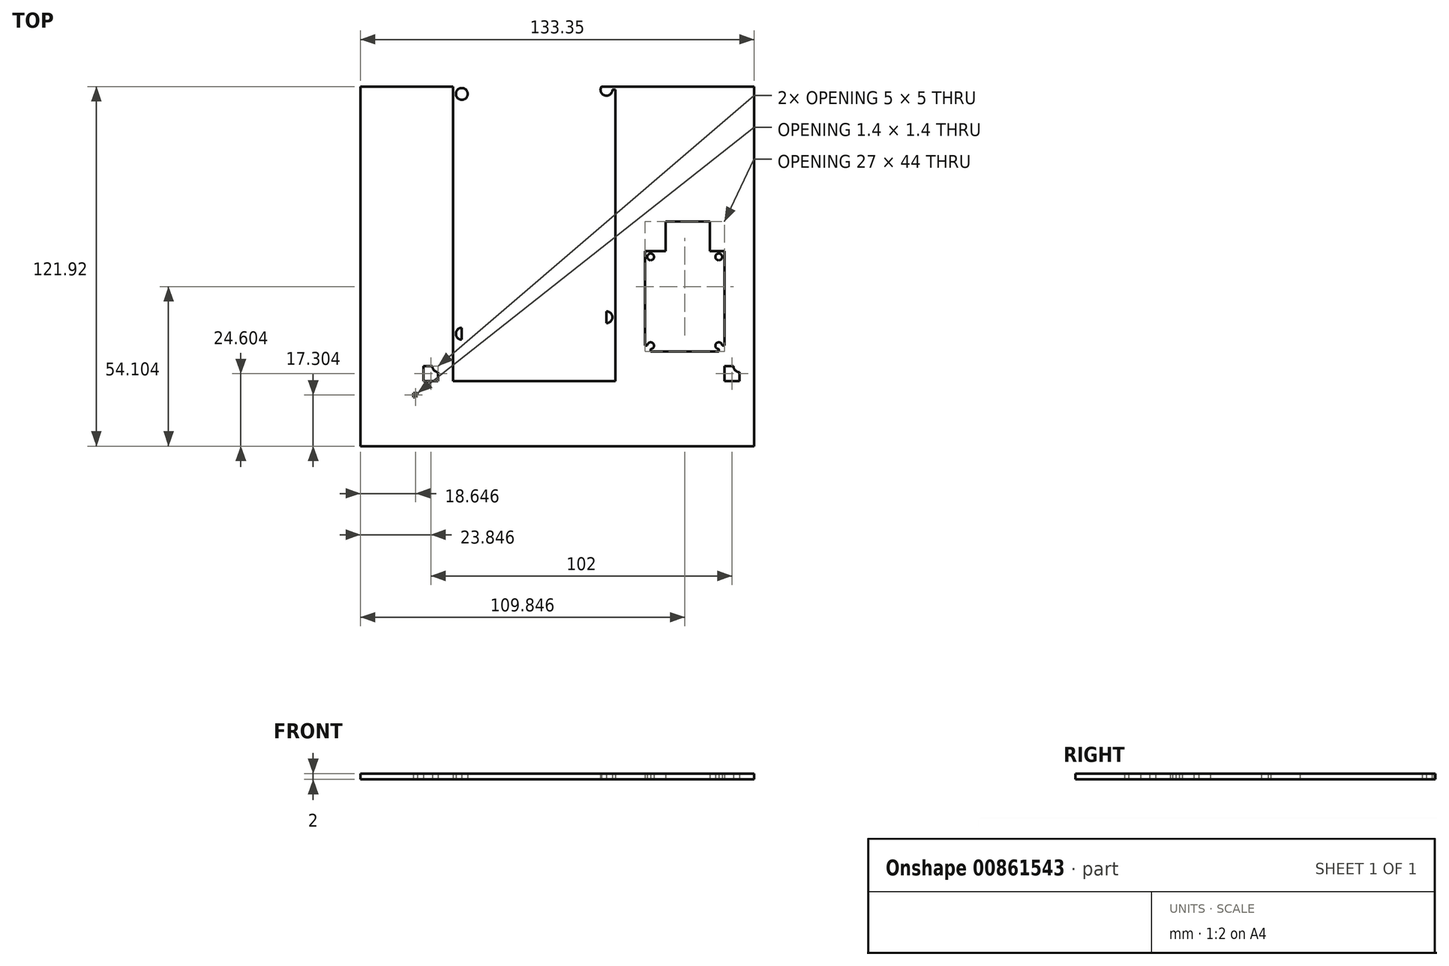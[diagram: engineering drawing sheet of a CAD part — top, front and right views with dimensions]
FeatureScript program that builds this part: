
annotation { "Feature Type Name" : "Feature", "Feature Type Description" : "" }
export const myFeature = defineFeature(function(context is Context, id is Id, definition is map)
    precondition{}
    {
        {
            var Q0;
            Q0=qCreatedBy(makeId("Top.planeOp"),FACE);
            var sketch = newSketch(context, id + "F0", { "sketchPlane" : qUnion([Q0])});
            skLineSegment(sketch, "E0.bottom", {"start": v(-139.34, -1.26) * mm, "end": v(-129.34, -1.26) * mm});
            skLineSegment(sketch, "E0.top", {"start": v(-139.34, -11.26) * mm, "end": v(-129.34, -11.26) * mm});
            skLineSegment(sketch, "E0.left", {"start": v(-139.34, -1.26) * mm, "end": v(-139.34, -11.26) * mm});
            skLineSegment(sketch, "E0.right", {"start": v(-129.34, -1.26) * mm, "end": v(-129.34, -11.26) * mm});
            skLineSegment(sketch, "E1.bottom", {"start": v(-129.34, -11.26) * mm, "end": v(-74.34, -11.26) * mm});
            skLineSegment(sketch, "E1.top", {"start": v(-129.34, -114.76) * mm, "end": v(-74.34, -114.76) * mm});
            skLineSegment(sketch, "E1.left", {"start": v(-129.34, -11.26) * mm, "end": v(-129.34, -114.76) * mm});
            skLineSegment(sketch, "E1.right", {"start": v(-74.34, -11.26) * mm, "end": v(-74.34, -114.76) * mm});
            skLineSegment(sketch, "E2", {"start": v(-74.34, -114.76) * mm, "end": v(-64.34, -114.76) * mm});
            skLineSegment(sketch, "E3.bottom", {"start": v(-64.34, -114.76) * mm, "end": v(-37.34, -114.76) * mm});
            skLineSegment(sketch, "E3.top", {"start": v(-64.34, -80.76) * mm, "end": v(-37.34, -80.76) * mm});
            skLineSegment(sketch, "E3.left", {"start": v(-64.34, -114.76) * mm, "end": v(-64.34, -80.76) * mm});
            skLineSegment(sketch, "E3.right", {"start": v(-37.34, -114.76) * mm, "end": v(-37.34, -80.76) * mm});
            skLineSegment(sketch, "E4", {"start": v(-37.34, -80.76) * mm, "end": v(-42.34, -80.76) * mm});
            skLineSegment(sketch, "E5.bottom", {"start": v(-42.34, -80.76) * mm, "end": v(-57.34, -80.76) * mm});
            skLineSegment(sketch, "E5.top", {"start": v(-42.34, -70.76) * mm, "end": v(-57.34, -70.76) * mm});
            skLineSegment(sketch, "E5.left", {"start": v(-42.34, -80.76) * mm, "end": v(-42.34, -70.76) * mm});
            skLineSegment(sketch, "E5.right", {"start": v(-57.34, -80.76) * mm, "end": v(-57.34, -70.76) * mm});
            skLineSegment(sketch, "E6", {"start": v(-64.34, -80.76) * mm, "end": v(-64.34, -60.76) * mm});
            skLineSegment(sketch, "E7.bottom", {"start": v(-64.34, -60.76) * mm, "end": v(-37.84, -60.76) * mm});
            skLineSegment(sketch, "E7.top", {"start": v(-64.34, -24.76) * mm, "end": v(-37.84, -24.76) * mm});
            skLineSegment(sketch, "E7.left", {"start": v(-64.34, -60.76) * mm, "end": v(-64.34, -24.76) * mm});
            skLineSegment(sketch, "E7.right", {"start": v(-37.84, -60.76) * mm, "end": v(-37.84, -24.76) * mm});
            skLineSegment(sketch, "E8", {"start": v(-74.34, -11.26) * mm, "end": v(-27.34, -11.26) * mm});
            skLineSegment(sketch, "E9.bottom", {"start": v(-129.34, -114.76) * mm, "end": v(-139.34, -114.76) * mm});
            skLineSegment(sketch, "E9.top", {"start": v(-129.34, -124.76) * mm, "end": v(-139.34, -124.76) * mm});
            skLineSegment(sketch, "E9.left", {"start": v(-129.34, -114.76) * mm, "end": v(-129.34, -124.76) * mm});
            skLineSegment(sketch, "E9.right", {"start": v(-139.34, -114.76) * mm, "end": v(-139.34, -124.76) * mm});
            skLineSegment(sketch, "E10.bottom", {"start": v(-37.34, -114.76) * mm, "end": v(-27.34, -114.76) * mm});
            skLineSegment(sketch, "E10.top", {"start": v(-37.34, -124.76) * mm, "end": v(-27.34, -124.76) * mm});
            skLineSegment(sketch, "E10.left", {"start": v(-37.34, -114.76) * mm, "end": v(-37.34, -124.76) * mm});
            skLineSegment(sketch, "E10.right", {"start": v(-27.34, -114.76) * mm, "end": v(-27.34, -124.76) * mm});
            skLineSegment(sketch, "E11.top", {"start": v(-139.34, -124.76) * mm, "end": v(-37.34, -124.76) * mm});
            skLineSegment(sketch, "E12", {"start": v(-129.34, -11.26) * mm, "end": v(-124.34, -11.26) * mm});
            skLineSegment(sketch, "E13", {"start": v(-124.34, -11.26) * mm, "end": v(-124.34, -1.26) * mm});
            skLineSegment(sketch, "E14", {"start": v(-74.34, -11.26) * mm, "end": v(-79.34, -11.26) * mm});
            skLineSegment(sketch, "E15", {"start": v(-79.34, -11.26) * mm, "end": v(-79.34, -1.26) * mm});
            skLineSegment(sketch, "E16.bottom", {"start": v(-129.34, -11.26) * mm, "end": v(-126.54, -11.26) * mm});
            skLineSegment(sketch, "E16.left", {"start": v(-129.34, -11.26) * mm, "end": v(-129.34, -14.06) * mm});
            skLineSegment(sketch, "E17.bottom", {"start": v(-129.34, -114.76) * mm, "end": v(-126.34, -114.76) * mm});
            skLineSegment(sketch, "E17.left", {"start": v(-129.34, -114.76) * mm, "end": v(-129.34, -111.76) * mm});
            skLineSegment(sketch, "E18.bottom", {"start": v(-74.34, -114.76) * mm, "end": v(-77.2, -114.76) * mm});
            skLineSegment(sketch, "E18.left", {"start": v(-74.34, -114.76) * mm, "end": v(-74.34, -111.9) * mm});
            skLineSegment(sketch, "E19.bottom", {"start": v(-74.34, -11.26) * mm, "end": v(-77.34, -11.26) * mm});
            skLineSegment(sketch, "E19.left", {"start": v(-74.34, -11.26) * mm, "end": v(-74.34, -14.26) * mm});
            skLineSegment(sketch, "E20.left", {"start": v(-27.34, -11.26) * mm, "end": v(-27.34, -14.66) * mm});
            skLineSegment(sketch, "E21.bottom", {"start": v(-37.84, -60.76) * mm, "end": v(-39.6, -60.76) * mm});
            skLineSegment(sketch, "E21.left", {"start": v(-37.84, -60.76) * mm, "end": v(-37.84, -59) * mm});
            skLineSegment(sketch, "E22.bottom", {"start": v(-37.84, -24.76) * mm, "end": v(-39.54, -24.76) * mm});
            skLineSegment(sketch, "E22.top", {"start": v(-37.84, -26.46) * mm, "end": v(-39.54, -26.46) * mm});
            skLineSegment(sketch, "E22.left", {"start": v(-37.84, -24.76) * mm, "end": v(-37.84, -26.46) * mm});
            skLineSegment(sketch, "E22.right", {"start": v(-39.54, -24.76) * mm, "end": v(-39.54, -26.46) * mm});
            skLineSegment(sketch, "E23.bottom", {"start": v(-64.34, -24.76) * mm, "end": v(-62.64, -24.76) * mm});
            skLineSegment(sketch, "E23.top", {"start": v(-64.34, -26.46) * mm, "end": v(-62.64, -26.46) * mm});
            skLineSegment(sketch, "E23.left", {"start": v(-64.34, -24.76) * mm, "end": v(-64.34, -26.46) * mm});
            skLineSegment(sketch, "E23.right", {"start": v(-62.64, -24.76) * mm, "end": v(-62.64, -26.46) * mm});
            skLineSegment(sketch, "E24.bottom", {"start": v(-64.34, -60.76) * mm, "end": v(-62.6, -60.76) * mm});
            skLineSegment(sketch, "E24.left", {"start": v(-64.34, -60.76) * mm, "end": v(-64.34, -59) * mm});
            skLineSegment(sketch, "E25.bottom", {"start": v(-64.34, -114.76) * mm, "end": v(-62.4, -114.76) * mm});
            skLineSegment(sketch, "E25.top", {"start": v(-64.34, -112.8) * mm, "end": v(-62.4, -112.8) * mm});
            skLineSegment(sketch, "E25.left", {"start": v(-64.34, -114.76) * mm, "end": v(-64.34, -112.8) * mm});
            skLineSegment(sketch, "E25.right", {"start": v(-62.4, -114.76) * mm, "end": v(-62.4, -112.8) * mm});
            skLineSegment(sketch, "E26.bottom", {"start": v(-37.34, -114.76) * mm, "end": v(-39.3, -114.76) * mm});
            skLineSegment(sketch, "E26.top", {"start": v(-37.34, -112.8) * mm, "end": v(-39.3, -112.8) * mm});
            skLineSegment(sketch, "E26.left", {"start": v(-37.34, -114.76) * mm, "end": v(-37.34, -112.8) * mm});
            skLineSegment(sketch, "E26.right", {"start": v(-39.3, -114.76) * mm, "end": v(-39.3, -112.8) * mm});
            skLineSegment(sketch, "E27.bottom", {"start": v(-37.34, -80.76) * mm, "end": v(-39.3, -80.76) * mm});
            skLineSegment(sketch, "E27.top", {"start": v(-37.34, -82.7) * mm, "end": v(-39.3, -82.7) * mm});
            skLineSegment(sketch, "E27.left", {"start": v(-37.34, -80.76) * mm, "end": v(-37.34, -82.7) * mm});
            skLineSegment(sketch, "E27.right", {"start": v(-39.3, -80.76) * mm, "end": v(-39.3, -82.7) * mm});
            skLineSegment(sketch, "E28.bottom", {"start": v(-64.34, -80.76) * mm, "end": v(-62.4, -80.76) * mm});
            skLineSegment(sketch, "E28.top", {"start": v(-64.34, -82.7) * mm, "end": v(-62.4, -82.7) * mm});
            skLineSegment(sketch, "E28.left", {"start": v(-64.34, -80.76) * mm, "end": v(-64.34, -82.7) * mm});
            skLineSegment(sketch, "E28.right", {"start": v(-62.4, -80.76) * mm, "end": v(-62.4, -82.7) * mm});
            skCircle(sketch, "E29", {"center": v(-39.3, -112.8) * mm, "radius": 1.15 * mm});
            skCircle(sketch, "E30", {"center": v(-62.4, -112.8) * mm, "radius": 1.15 * mm});
            skCircle(sketch, "E31", {"center": v(-62.4, -82.7) * mm, "radius": 1.15 * mm});
            skCircle(sketch, "E32", {"center": v(-39.3, -82.7) * mm, "radius": 1.15 * mm});
            skCircle(sketch, "E33", {"center": v(-62.64, -26.46) * mm, "radius": 1.2 * mm});
            skCircle(sketch, "E34", {"center": v(-39.54, -26.46) * mm, "radius": 1.2 * mm});
            skLineSegment(sketch, "E35.top", {"start": v(-37.34, -124.76) * mm, "end": v(-139.34, -124.76) * mm});
            skLineSegment(sketch, "E36.bottom", {"start": v(-139.34, -124.76) * mm, "end": v(-134.34, -124.76) * mm});
            skLineSegment(sketch, "E36.top", {"start": v(-139.34, -119.76) * mm, "end": v(-134.34, -119.76) * mm});
            skLineSegment(sketch, "E36.left", {"start": v(-139.34, -124.76) * mm, "end": v(-139.34, -119.76) * mm});
            skLineSegment(sketch, "E36.right", {"start": v(-134.34, -124.76) * mm, "end": v(-134.34, -119.76) * mm});
            skCircle(sketch, "E37", {"center": v(-134.34, -119.76) * mm, "radius": 2 * mm});
            skLineSegment(sketch, "E38.bottom", {"start": v(-37.34, -124.76) * mm, "end": v(-32.34, -124.76) * mm});
            skLineSegment(sketch, "E38.top", {"start": v(-37.34, -119.76) * mm, "end": v(-32.34, -119.76) * mm});
            skLineSegment(sketch, "E38.left", {"start": v(-37.34, -124.76) * mm, "end": v(-37.34, -119.76) * mm});
            skLineSegment(sketch, "E38.right", {"start": v(-32.34, -124.76) * mm, "end": v(-32.34, -119.76) * mm});
            skCircle(sketch, "E39", {"center": v(-32.34, -119.76) * mm, "radius": 2 * mm});
            skLineSegment(sketch, "E40.bottom", {"start": v(-139.34, -1.26) * mm, "end": v(-134.34, -1.26) * mm});
            skLineSegment(sketch, "E40.top", {"start": v(-139.34, -6.26) * mm, "end": v(-134.34, -6.26) * mm});
            skLineSegment(sketch, "E40.left", {"start": v(-139.34, -1.26) * mm, "end": v(-139.34, -6.26) * mm});
            skLineSegment(sketch, "E40.right", {"start": v(-134.34, -1.26) * mm, "end": v(-134.34, -6.26) * mm});
            skCircle(sketch, "E41", {"center": v(-134.34, -6.26) * mm, "radius": 2 * mm});
            skLineSegment(sketch, "E42.bottom", {"start": v(-129.34, -11.26) * mm, "end": v(-126.34, -11.26) * mm});
            skLineSegment(sketch, "E42.left", {"start": v(-129.34, -11.26) * mm, "end": v(-129.34, -27.96) * mm});
            skLineSegment(sketch, "E43.top", {"start": v(-129.34, -108.76) * mm, "end": v(-126.34, -108.76) * mm});
            skLineSegment(sketch, "E43.left", {"start": v(-129.34, -114.76) * mm, "end": v(-129.34, -108.76) * mm});
            skLineSegment(sketch, "E43.right", {"start": v(-126.34, -114.76) * mm, "end": v(-126.34, -108.76) * mm});
            skLineSegment(sketch, "E44.bottom", {"start": v(-74.34, -114.76) * mm, "end": v(-77.34, -114.76) * mm});
            skLineSegment(sketch, "E44.top", {"start": v(-74.34, -103.16) * mm, "end": v(-77.34, -103.16) * mm});
            skLineSegment(sketch, "E44.left", {"start": v(-74.34, -114.76) * mm, "end": v(-74.34, -103.16) * mm});
            skLineSegment(sketch, "E44.right", {"start": v(-77.34, -114.76) * mm, "end": v(-77.34, -103.16) * mm});
            skLineSegment(sketch, "E45.top", {"start": v(-74.34, -26.06) * mm, "end": v(-77.34, -26.06) * mm});
            skLineSegment(sketch, "E45.left", {"start": v(-74.34, -114.76) * mm, "end": v(-74.34, -26.06) * mm});
            skLineSegment(sketch, "E45.right", {"start": v(-77.34, -114.76) * mm, "end": v(-77.34, -26.06) * mm});
            skLineSegment(sketch, "E46.top", {"start": v(-129.34, -27.46) * mm, "end": v(-126.34, -27.46) * mm});
            skLineSegment(sketch, "E46.left", {"start": v(-129.34, -114.76) * mm, "end": v(-129.34, -27.46) * mm});
            skLineSegment(sketch, "E46.right", {"start": v(-126.34, -114.76) * mm, "end": v(-126.34, -27.46) * mm});
            skCircle(sketch, "E47", {"center": v(-126.34, -108.76) * mm, "radius": 2 * mm});
            skCircle(sketch, "E48", {"center": v(-126.34, -27.46) * mm, "radius": 2 * mm});
            skCircle(sketch, "E49", {"center": v(-77.34, -26.06) * mm, "radius": 2 * mm});
            skCircle(sketch, "E50", {"center": v(-77.34, -103.16) * mm, "radius": 2 * mm});
            skLineSegment(sketch, "E51", {"start": v(-139.34, -1.26) * mm, "end": v(-83.34, -1.26) * mm});
            skLineSegment(sketch, "E52.bottom", {"start": v(-83.34, -1.26) * mm, "end": v(-139.34, -1.26) * mm});
            skLineSegment(sketch, "E53.MirrorCS", {"start": v(-139.5, -132.26) * mm, "end": v(-139.5, -11.26) * mm});
            skLineSegment(sketch, "E54.MirrorCS", {"start": v(-221.34, -11.26) * mm, "end": v(-139.34, -11.26) * mm});
            skLineSegment(sketch, "E55.MirrorCS", {"start": v(-221.34, -132.26) * mm, "end": v(-139.34, -132.26) * mm});
            skCircle(sketch, "E56.MirrorC", {"center": v(-142.74, -128.86) * mm, "radius": 1.4 * mm});
            skCircle(sketch, "E57.MirrorC", {"center": v(-217.94, -128.86) * mm, "radius": 1.7 * mm});
            skCircle(sketch, "E58.MirrorC", {"center": v(-217.94, -14.66) * mm, "radius": 1.4 * mm});
            skCircle(sketch, "E59.MirrorC", {"center": v(-142.74, -14.66) * mm, "radius": 1.4 * mm});
            skLineSegment(sketch, "E60.MirrorCS", {"start": v(-142.74, -11.26) * mm, "end": v(-142.74, -14.66) * mm});
            skLineSegment(sketch, "E61.MirrorCS", {"start": v(-139.34, -14.66) * mm, "end": v(-142.74, -14.66) * mm});
            skLineSegment(sketch, "E62.MirrorCS", {"start": v(-217.94, -11.26) * mm, "end": v(-217.94, -14.66) * mm});
            skLineSegment(sketch, "E63.MirrorCS", {"start": v(-221.34, -14.66) * mm, "end": v(-217.94, -14.66) * mm});
            skLineSegment(sketch, "E64.MirrorCS", {"start": v(-142.74, -132.26) * mm, "end": v(-142.74, -128.86) * mm});
            skLineSegment(sketch, "E65.MirrorCS", {"start": v(-139.34, -128.86) * mm, "end": v(-142.74, -128.86) * mm});
            skLineSegment(sketch, "E66.MirrorCS", {"start": v(-221.34, -128.86) * mm, "end": v(-217.94, -128.86) * mm});
            skLineSegment(sketch, "E67.MirrorCS", {"start": v(-217.94, -132.26) * mm, "end": v(-217.94, -128.86) * mm});
            skLineSegment(sketch, "E68.MirrorCS", {"start": v(-27.34, -1.26) * mm, "end": v(-231.34, -1.26) * mm});
            skLineSegment(sketch, "E69", {"start": v(-221.34, -11.26) * mm, "end": v(-221.34, -1.26) * mm});
            skLineSegment(sketch, "E70", {"start": v(-221.34, -132.26) * mm, "end": v(-221.34, -11.26) * mm});
            skLineSegment(sketch, "E71", {"start": v(-221.34, -132.26) * mm, "end": v(-231.5, -132.26) * mm});
            skLineSegment(sketch, "E72", {"start": v(-27.34, -11.26) * mm, "end": v(-27.34, -1.26) * mm});
            skLineSegment(sketch, "E73.bottom", {"start": v(-221.34, -132.26) * mm, "end": v(-231.34, -132.26) * mm});
            skLineSegment(sketch, "E73.top", {"start": v(-221.34, -142.26) * mm, "end": v(-231.34, -142.26) * mm});
            skLineSegment(sketch, "E73.left", {"start": v(-221.34, -132.26) * mm, "end": v(-221.34, -142.26) * mm});
            skLineSegment(sketch, "E73.right", {"start": v(-231.34, -132.26) * mm, "end": v(-231.34, -142.26) * mm});
            skLineSegment(sketch, "E74.bottom", {"start": v(-221.34, -142.26) * mm, "end": v(-139.34, -142.26) * mm});
            skLineSegment(sketch, "E74.left", {"start": v(-221.34, -142.26) * mm, "end": v(-221.34, -132.26) * mm});
            skLineSegment(sketch, "E75", {"start": v(-27.34, -114.76) * mm, "end": v(-27.34, -11.26) * mm});
            skLineSegment(sketch, "E76", {"start": v(-231.34, -132.26) * mm, "end": v(-231.34, -1.26) * mm});
            skLineSegment(sketch, "E77.bottom", {"start": v(-129.34, -124.76) * mm, "end": v(-139.2, -124.76) * mm});
            skLineSegment(sketch, "E77.top", {"start": v(-129.34, -142.26) * mm, "end": v(-139.34, -142.26) * mm});
            skLineSegment(sketch, "E77.left", {"start": v(-129.34, -124.76) * mm, "end": v(-129.34, -142.26) * mm});
            skLineSegment(sketch, "E78", {"start": v(-139.34, -142.26) * mm, "end": v(-139.5, -132.26) * mm});
            skLineSegment(sketch, "E79.bottom", {"start": v(-231.34, -142.26) * mm, "end": v(-226.34, -142.26) * mm});
            skLineSegment(sketch, "E79.top", {"start": v(-231.34, -137.4) * mm, "end": v(-226.34, -137.4) * mm});
            skLineSegment(sketch, "E79.left", {"start": v(-231.34, -142.26) * mm, "end": v(-231.34, -137.4) * mm});
            skLineSegment(sketch, "E79.right", {"start": v(-226.34, -142.26) * mm, "end": v(-226.34, -137.4) * mm});
            skCircle(sketch, "E80", {"center": v(-226.34, -137.4) * mm, "radius": 2 * mm});
            skLineSegment(sketch, "E81.bottom", {"start": v(-221.34, -11.26) * mm, "end": v(-226.34, -11.26) * mm});
            skLineSegment(sketch, "E81.top", {"start": v(-221.34, -6.26) * mm, "end": v(-226.34, -6.26) * mm});
            skLineSegment(sketch, "E81.left", {"start": v(-221.34, -11.26) * mm, "end": v(-221.34, -6.26) * mm});
            skLineSegment(sketch, "E81.right", {"start": v(-226.34, -11.26) * mm, "end": v(-226.34, -6.26) * mm});
            skCircle(sketch, "E82", {"center": v(-226.34, -6.26) * mm, "radius": 2 * mm});
            skLineSegment(sketch, "E83.bottom", {"start": v(-27.34, -11.26) * mm, "end": v(-32.34, -11.26) * mm});
            skLineSegment(sketch, "E83.top", {"start": v(-27.34, -6.26) * mm, "end": v(-32.34, -6.26) * mm});
            skLineSegment(sketch, "E83.left", {"start": v(-27.34, -11.26) * mm, "end": v(-27.34, -6.26) * mm});
            skLineSegment(sketch, "E83.right", {"start": v(-32.34, -11.26) * mm, "end": v(-32.34, -6.26) * mm});
            skCircle(sketch, "E84", {"center": v(-32.34, -6.26) * mm, "radius": 2 * mm});
            skLineSegment(sketch, "E85.bottom", {"start": v(-129.34, -142.26) * mm, "end": v(-77.34, -142.26) * mm});
            skLineSegment(sketch, "E85.top", {"start": v(-129.34, -114.76) * mm, "end": v(-77.34, -114.76) * mm});
            skLineSegment(sketch, "E85.left", {"start": v(-129.34, -142.26) * mm, "end": v(-129.34, -114.76) * mm});
            skLineSegment(sketch, "E86.bottom", {"start": v(-129.34, -142.26) * mm, "end": v(-74.34, -142.26) * mm});
            skLineSegment(sketch, "E86.right", {"start": v(-74.34, -142.26) * mm, "end": v(-74.34, -114.76) * mm});
            skLineSegment(sketch, "E87", {"start": v(-37.84, -24.76) * mm, "end": v(-27.34, -24.94) * mm});
            skLineSegment(sketch, "E88.bottom", {"start": v(-27.34, -24.94) * mm, "end": v(-160.7, -24.94) * mm});
            skLineSegment(sketch, "E88.top", {"start": v(-27.34, -146.86) * mm, "end": v(-160.7, -146.86) * mm});
            skLineSegment(sketch, "E88.left", {"start": v(-27.34, -24.94) * mm, "end": v(-27.34, -146.86) * mm});
            skLineSegment(sketch, "E88.right", {"start": v(-160.7, -24.94) * mm, "end": v(-160.7, -146.86) * mm});
            skSolve(sketch);
        }
        {
            var Q0;
            {var subQ5=sQuery(id+"F0.wireOp",EDGE,"E65.MirrorCS");var subQ7=sQuery(id+"F0.wireOp",EDGE,"E53.MirrorCS");var subQ8=makeQuery(id+"F0.imprint","INTERSECT",VERTEX,{"derivedFrom":[subQ7,subQ5]});Q0=makeQuery(id+"F0.imprint","IMPRINT",FACE,{"disambiguationData":[TD([[makeQuery(id+"F0.imprint","IMPRINT",EDGE,{"disambiguationData":[TD([[subQ8,-1.0]])],"derivedFrom":subQ7}),1.0]])]});}
            var Q1;
            {var subQ1=sQuery(id+"F0.wireOp",EDGE,"E45.right");var subQ16=sQuery(id+"F0.wireOp",EDGE,"E1.top");var subQ17=makeQuery(id+"F0.imprint","INTERSECT",VERTEX,{"derivedFrom":[subQ1,subQ16]});Q1=makeQuery(id+"F0.imprint","IMPRINT",FACE,{"disambiguationData":[TD([[makeQuery(id+"F0.imprint","IMPRINT",EDGE,{"disambiguationData":[TD([[subQ17,-1.0]])],"derivedFrom":subQ1}),1.0]])]});}
            var Q2;
            {var subQ6=sQuery(id+"F0.wireOp",EDGE,"E9.bottom");Q2=makeQuery(id+"F0.imprint","IMPRINT",FACE,{"disambiguationData":[TD([[makeQuery(id+"F0.imprint","IMPRINT",EDGE,{"derivedFrom":subQ6}),-1.0]])]});}
            var Q3;
            {var subQ0=sQuery(id+"F0.wireOp",EDGE,"E46.left");var subQ3=makeQuery(id+"F0.imprint","IMPRINT",VERTEX,{"disambiguationData":[OD(1.0)],"derivedFrom":subQ0});Q3=makeQuery(id+"F0.imprint","IMPRINT",FACE,{"disambiguationData":[TD([[makeQuery(id+"F0.imprint","IMPRINT",EDGE,{"disambiguationData":[TD([[subQ3,1.0]])],"derivedFrom":subQ0}),-1.0]])]});}
            var Q4;
            {var subQ0=sQuery(id+"F0.wireOp",EDGE,"E46.right");var subQ1=sQuery(id+"F0.wireOp",EDGE,"E46.top");var subQ2=makeQuery(id+"F0.imprint","INTERSECT",VERTEX,{"derivedFrom":[subQ1,subQ0]});Q4=makeQuery(id+"F0.imprint","IMPRINT",FACE,{"disambiguationData":[TD([[makeQuery(id+"F0.imprint","IMPRINT",EDGE,{"disambiguationData":[TD([[subQ2,1.0]])],"derivedFrom":subQ1}),1.0]])]});}
            var Q5;
            {var subQ0=sQuery(id+"F0.wireOp",EDGE,"E46.right");var subQ1=sQuery(id+"F0.wireOp",EDGE,"E46.top");var subQ2=makeQuery(id+"F0.imprint","INTERSECT",VERTEX,{"derivedFrom":[subQ1,subQ0]});Q5=makeQuery(id+"F0.imprint","IMPRINT",FACE,{"disambiguationData":[TD([[makeQuery(id+"F0.imprint","IMPRINT",EDGE,{"disambiguationData":[TD([[subQ2,1.0]])],"derivedFrom":subQ1}),-1.0]])]});}
            var Q6;
            {var subQ1=sQuery(id+"F0.wireOp",EDGE,"E45.right");var subQ5=sQuery(id+"F0.wireOp",EDGE,"E45.top");var subQ6=makeQuery(id+"F0.imprint","INTERSECT",VERTEX,{"derivedFrom":[subQ5,subQ1]});Q6=makeQuery(id+"F0.imprint","IMPRINT",FACE,{"disambiguationData":[TD([[makeQuery(id+"F0.imprint","IMPRINT",EDGE,{"disambiguationData":[TD([[subQ6,1.0]])],"derivedFrom":subQ5}),-1.0]])]});}
            var Q7;
            {var subQ0=sQuery(id+"F0.wireOp",EDGE,"E45.left");var subQ3=sQuery(id+"F0.wireOp",EDGE,"E44.top");var subQ4=makeQuery(id+"F0.imprint","INTERSECT",VERTEX,{"derivedFrom":[subQ3,subQ0]});Q7=makeQuery(id+"F0.imprint","IMPRINT",FACE,{"disambiguationData":[TD([[makeQuery(id+"F0.imprint","IMPRINT",EDGE,{"disambiguationData":[TD([[subQ4,-1.0]])],"derivedFrom":subQ3}),-1.0]])]});}
            var Q8;
            {var subQ1=sQuery(id+"F0.wireOp",EDGE,"E2");Q8=makeQuery(id+"F0.imprint","IMPRINT",FACE,{"disambiguationData":[TD([[makeQuery(id+"F0.imprint","IMPRINT",EDGE,{"derivedFrom":subQ1}),1.0]])]});}
            var Q9;
            {var subQ0=sQuery(id+"F0.wireOp",EDGE,"E45.right");var subQ1=sQuery(id+"F0.wireOp",EDGE,"E45.top");var subQ2=makeQuery(id+"F0.imprint","INTERSECT",VERTEX,{"derivedFrom":[subQ1,subQ0]});Q9=makeQuery(id+"F0.imprint","IMPRINT",FACE,{"disambiguationData":[TD([[makeQuery(id+"F0.imprint","IMPRINT",EDGE,{"disambiguationData":[TD([[subQ2,1.0]])],"derivedFrom":subQ1}),1.0]])]});}
            var Q10;
            Q10=makeQuery(id+"F0.imprint","IMPRINT",FACE,{"disambiguationData":[TD([[makeQuery(id+"F0.imprint","IMPRINT",EDGE,{"derivedFrom":sQuery(id+"F0.wireOp",EDGE,"E7.bottom")}),1.0]])]});
            var Q11;
            {var subQ0=sQuery(id+"F0.wireOp",EDGE,"E23.right");var subQ1=sQuery(id+"F0.wireOp",EDGE,"E23.top");var subQ2=makeQuery(id+"F0.imprint","INTERSECT",VERTEX,{"derivedFrom":[subQ1,subQ0]});Q11=makeQuery(id+"F0.imprint","IMPRINT",FACE,{"disambiguationData":[TD([[makeQuery(id+"F0.imprint","IMPRINT",EDGE,{"disambiguationData":[TD([[subQ2,1.0]])],"derivedFrom":subQ1}),-1.0]])]});}
            var Q12;
            {var subQ0=sQuery(id+"F0.wireOp",EDGE,"E23.right");var subQ1=sQuery(id+"F0.wireOp",EDGE,"E23.top");var subQ2=makeQuery(id+"F0.imprint","INTERSECT",VERTEX,{"derivedFrom":[subQ1,subQ0]});Q12=makeQuery(id+"F0.imprint","IMPRINT",FACE,{"disambiguationData":[TD([[makeQuery(id+"F0.imprint","IMPRINT",EDGE,{"disambiguationData":[TD([[subQ2,1.0]])],"derivedFrom":subQ1}),1.0]])]});}
            var Q13;
            {var subQ3=sQuery(id+"F0.wireOp",EDGE,"E23.right");var subQ7=sQuery(id+"F0.wireOp",EDGE,"E88.bottom");var subQ9=makeQuery(id+"F0.imprint","INTERSECT",VERTEX,{"derivedFrom":[subQ3,subQ7]});Q13=makeQuery(id+"F0.imprint","IMPRINT",FACE,{"disambiguationData":[TD([[makeQuery(id+"F0.imprint","IMPRINT",EDGE,{"disambiguationData":[TD([[subQ9,-1.0]])],"derivedFrom":subQ3}),-1.0]])]});}
            var Q14;
            {var subQ0=sQuery(id+"F0.wireOp",EDGE,"E45.top");var subQ5=sQuery(id+"F0.wireOp",EDGE,"E49");var subQ6=makeQuery(id+"F0.imprint","INTERSECT",VERTEX,{"derivedFrom":[subQ0,subQ5]});Q14=makeQuery(id+"F0.imprint","IMPRINT",FACE,{"disambiguationData":[TD([[makeQuery(id+"F0.imprint","IMPRINT",EDGE,{"disambiguationData":[TD([[subQ6,-1.0]])],"derivedFrom":subQ5}),-1.0]])]});}
            var Q15;
            {var subQ3=sQuery(id+"F0.wireOp",EDGE,"E22.right");var subQ5=sQuery(id+"F0.wireOp",EDGE,"E88.bottom");var subQ8=makeQuery(id+"F0.imprint","INTERSECT",VERTEX,{"derivedFrom":[subQ3,subQ5]});Q15=makeQuery(id+"F0.imprint","IMPRINT",FACE,{"disambiguationData":[TD([[makeQuery(id+"F0.imprint","IMPRINT",EDGE,{"disambiguationData":[TD([[subQ8,-1.0]])],"derivedFrom":subQ3}),1.0]])]});}
            var Q16;
            {var subQ0=sQuery(id+"F0.wireOp",EDGE,"E22.right");var subQ1=sQuery(id+"F0.wireOp",EDGE,"E22.top");var subQ2=makeQuery(id+"F0.imprint","INTERSECT",VERTEX,{"derivedFrom":[subQ1,subQ0]});Q16=makeQuery(id+"F0.imprint","IMPRINT",FACE,{"disambiguationData":[TD([[makeQuery(id+"F0.imprint","IMPRINT",EDGE,{"disambiguationData":[TD([[subQ2,1.0]])],"derivedFrom":subQ1}),-1.0]])]});}
            var Q17;
            {var subQ0=sQuery(id+"F0.wireOp",EDGE,"E22.right");var subQ1=sQuery(id+"F0.wireOp",EDGE,"E22.top");var subQ2=makeQuery(id+"F0.imprint","INTERSECT",VERTEX,{"derivedFrom":[subQ1,subQ0]});Q17=makeQuery(id+"F0.imprint","IMPRINT",FACE,{"disambiguationData":[TD([[makeQuery(id+"F0.imprint","IMPRINT",EDGE,{"disambiguationData":[TD([[subQ2,1.0]])],"derivedFrom":subQ1}),1.0]])]});}
            var Q18;
            Q18=makeQuery(id+"F0.imprint","IMPRINT",FACE,{"disambiguationData":[TD([[makeQuery(id+"F0.imprint","IMPRINT",EDGE,{"derivedFrom":sQuery(id+"F0.wireOp",EDGE,"E3.top")}),1.0]])]});
            var Q19;
            {var subQ5=sQuery(id+"F0.wireOp",EDGE,"E45.left");var subQ7=makeQuery(id+"F0.imprint","IMPRINT",VERTEX,{"derivedFrom":subQ5});Q19=makeQuery(id+"F0.imprint","IMPRINT",FACE,{"disambiguationData":[TD([[makeQuery(id+"F0.imprint","IMPRINT",EDGE,{"disambiguationData":[TD([[subQ7,-1.0]])],"derivedFrom":subQ5}),1.0]])]});}
            var Q20;
            {var subQ0=sQuery(id+"F0.wireOp",EDGE,"E45.right");var subQ1=sQuery(id+"F0.wireOp",EDGE,"E44.top");var subQ2=makeQuery(id+"F0.imprint","INTERSECT",VERTEX,{"derivedFrom":[subQ1,subQ0]});Q20=makeQuery(id+"F0.imprint","IMPRINT",FACE,{"disambiguationData":[TD([[makeQuery(id+"F0.imprint","IMPRINT",EDGE,{"disambiguationData":[TD([[subQ2,1.0]])],"derivedFrom":subQ1}),1.0]])]});}
            var Q21;
            {var subQ0=sQuery(id+"F0.wireOp",EDGE,"E45.right");var subQ1=sQuery(id+"F0.wireOp",EDGE,"E44.top");var subQ2=makeQuery(id+"F0.imprint","INTERSECT",VERTEX,{"derivedFrom":[subQ1,subQ0]});Q21=makeQuery(id+"F0.imprint","IMPRINT",FACE,{"disambiguationData":[TD([[makeQuery(id+"F0.imprint","IMPRINT",EDGE,{"disambiguationData":[TD([[subQ2,1.0]])],"derivedFrom":subQ1}),-1.0]])]});}
            var Q22;
            {var subQ0=sQuery(id+"F0.wireOp",EDGE,"E45.right");var subQ1=makeQuery(id+"F0.imprint","INTERSECT",VERTEX,{"derivedFrom":[sQuery(id+"F0.wireOp",EDGE,"E44.top"),subQ0]});Q22=makeQuery(id+"F0.imprint","IMPRINT",FACE,{"disambiguationData":[TD([[makeQuery(id+"F0.imprint","IMPRINT",EDGE,{"disambiguationData":[TD([[subQ1,1.0]])],"derivedFrom":subQ0}),1.0]])]});}
            var Q23;
            {var subQ5=sQuery(id+"F0.wireOp",EDGE,"E3.bottom");Q23=makeQuery(id+"F0.imprint","IMPRINT",FACE,{"disambiguationData":[TD([[makeQuery(id+"F0.imprint","IMPRINT",EDGE,{"derivedFrom":subQ5}),1.0]])]});}
            var Q24;
            {var subQ0=sQuery(id+"F0.wireOp",EDGE,"E28.right");var subQ1=sQuery(id+"F0.wireOp",EDGE,"E28.top");var subQ2=makeQuery(id+"F0.imprint","INTERSECT",VERTEX,{"derivedFrom":[subQ1,subQ0]});Q24=makeQuery(id+"F0.imprint","IMPRINT",FACE,{"disambiguationData":[TD([[makeQuery(id+"F0.imprint","IMPRINT",EDGE,{"disambiguationData":[TD([[subQ2,1.0]])],"derivedFrom":subQ1}),-1.0]])]});}
            var Q25;
            {var subQ1=sQuery(id+"F0.wireOp",EDGE,"E28.bottom");Q25=makeQuery(id+"F0.imprint","IMPRINT",FACE,{"disambiguationData":[TD([[makeQuery(id+"F0.imprint","IMPRINT",EDGE,{"derivedFrom":subQ1}),-1.0]])]});}
            var Q26;
            {var subQ0=sQuery(id+"F0.wireOp",EDGE,"E28.right");var subQ1=sQuery(id+"F0.wireOp",EDGE,"E28.top");var subQ2=makeQuery(id+"F0.imprint","INTERSECT",VERTEX,{"derivedFrom":[subQ1,subQ0]});Q26=makeQuery(id+"F0.imprint","IMPRINT",FACE,{"disambiguationData":[TD([[makeQuery(id+"F0.imprint","IMPRINT",EDGE,{"disambiguationData":[TD([[subQ2,1.0]])],"derivedFrom":subQ1}),1.0]])]});}
            var Q27;
            Q27=makeQuery(id+"F0.imprint","IMPRINT",FACE,{"disambiguationData":[TD([[makeQuery(id+"F0.imprint","IMPRINT",EDGE,{"derivedFrom":sQuery(id+"F0.wireOp",EDGE,"E5.bottom")}),-1.0]])]});
            var Q28;
            {var subQ1=sQuery(id+"F0.wireOp",EDGE,"E27.bottom");Q28=makeQuery(id+"F0.imprint","IMPRINT",FACE,{"disambiguationData":[TD([[makeQuery(id+"F0.imprint","IMPRINT",EDGE,{"derivedFrom":subQ1}),1.0]])]});}
            var Q29;
            {var subQ0=sQuery(id+"F0.wireOp",EDGE,"E27.right");var subQ1=sQuery(id+"F0.wireOp",EDGE,"E27.top");var subQ2=makeQuery(id+"F0.imprint","INTERSECT",VERTEX,{"derivedFrom":[subQ1,subQ0]});Q29=makeQuery(id+"F0.imprint","IMPRINT",FACE,{"disambiguationData":[TD([[makeQuery(id+"F0.imprint","IMPRINT",EDGE,{"disambiguationData":[TD([[subQ2,1.0]])],"derivedFrom":subQ1}),-1.0]])]});}
            var Q30;
            {var subQ0=sQuery(id+"F0.wireOp",EDGE,"E27.right");var subQ1=sQuery(id+"F0.wireOp",EDGE,"E27.top");var subQ2=makeQuery(id+"F0.imprint","INTERSECT",VERTEX,{"derivedFrom":[subQ1,subQ0]});Q30=makeQuery(id+"F0.imprint","IMPRINT",FACE,{"disambiguationData":[TD([[makeQuery(id+"F0.imprint","IMPRINT",EDGE,{"disambiguationData":[TD([[subQ2,1.0]])],"derivedFrom":subQ1}),1.0]])]});}
            var Q31;
            {var subQ6=sQuery(id+"F0.wireOp",EDGE,"E10.top");Q31=makeQuery(id+"F0.imprint","IMPRINT",FACE,{"disambiguationData":[TD([[makeQuery(id+"F0.imprint","IMPRINT",EDGE,{"derivedFrom":subQ6}),-1.0]])]});}
            var Q32;
            {var subQ0=sQuery(id+"F0.wireOp",EDGE,"E78");Q32=makeQuery(id+"F0.imprint","IMPRINT",FACE,{"disambiguationData":[TD([[makeQuery(id+"F0.imprint","IMPRINT",EDGE,{"derivedFrom":subQ0}),1.0]])]});}
            var Q33;
            {var subQ3=sQuery(id+"F0.wireOp",EDGE,"E56.MirrorC");var subQ6=sQuery(id+"F0.wireOp",EDGE,"E64.MirrorCS");var subQ8=makeQuery(id+"F0.imprint","INTERSECT",VERTEX,{"derivedFrom":[subQ3,subQ6]});Q33=makeQuery(id+"F0.imprint","IMPRINT",FACE,{"disambiguationData":[TD([[makeQuery(id+"F0.imprint","IMPRINT",EDGE,{"disambiguationData":[TD([[subQ8,1.0]])],"derivedFrom":subQ3}),1.0]])]});}
            var Q34;
            {var subQ0=sQuery(id+"F0.wireOp",EDGE,"E64.MirrorCS");var subQ1=sQuery(id+"F0.wireOp",EDGE,"E56.MirrorC");var subQ2=makeQuery(id+"F0.imprint","INTERSECT",VERTEX,{"derivedFrom":[subQ1,subQ0]});Q34=makeQuery(id+"F0.imprint","IMPRINT",FACE,{"disambiguationData":[TD([[makeQuery(id+"F0.imprint","IMPRINT",EDGE,{"disambiguationData":[TD([[subQ2,1.0]])],"derivedFrom":subQ1}),-1.0]])]});}
            var Q35;
            {var subQ0=sQuery(id+"F0.wireOp",EDGE,"E64.MirrorCS");var subQ1=sQuery(id+"F0.wireOp",EDGE,"E56.MirrorC");var subQ2=makeQuery(id+"F0.imprint","INTERSECT",VERTEX,{"derivedFrom":[subQ1,subQ0]});Q35=makeQuery(id+"F0.imprint","IMPRINT",FACE,{"disambiguationData":[TD([[makeQuery(id+"F0.imprint","IMPRINT",EDGE,{"disambiguationData":[TD([[subQ2,-1.0]])],"derivedFrom":subQ1}),-1.0]])]});}
            var Q36;
            {var subQ0=sQuery(id+"F0.wireOp",EDGE,"E36.right");var subQ1=sQuery(id+"F0.wireOp",EDGE,"E36.top");var subQ2=makeQuery(id+"F0.imprint","INTERSECT",VERTEX,{"derivedFrom":[subQ1,subQ0]});Q36=makeQuery(id+"F0.imprint","IMPRINT",FACE,{"disambiguationData":[TD([[makeQuery(id+"F0.imprint","IMPRINT",EDGE,{"disambiguationData":[TD([[subQ2,1.0]])],"derivedFrom":subQ1}),-1.0]])]});}
            var Q37;
            {var subQ0=sQuery(id+"F0.wireOp",EDGE,"E36.right");var subQ1=sQuery(id+"F0.wireOp",EDGE,"E36.top");var subQ2=makeQuery(id+"F0.imprint","INTERSECT",VERTEX,{"derivedFrom":[subQ1,subQ0]});Q37=makeQuery(id+"F0.imprint","IMPRINT",FACE,{"disambiguationData":[TD([[makeQuery(id+"F0.imprint","IMPRINT",EDGE,{"disambiguationData":[TD([[subQ2,1.0]])],"derivedFrom":subQ1}),1.0]])]});}
            var Q38;
            {var subQ8=sQuery(id+"F0.wireOp",EDGE,"E36.bottom");Q38=makeQuery(id+"F0.imprint","IMPRINT",FACE,{"disambiguationData":[TD([[makeQuery(id+"F0.imprint","IMPRINT",EDGE,{"derivedFrom":subQ8}),1.0]])]});}
            var Q39;
            {var subQ8=sQuery(id+"F0.wireOp",EDGE,"E9.bottom");Q39=makeQuery(id+"F0.imprint","IMPRINT",FACE,{"disambiguationData":[TD([[makeQuery(id+"F0.imprint","IMPRINT",EDGE,{"derivedFrom":subQ8}),1.0]])]});}
            var Q40;
            {var subQ0=sQuery(id+"F0.wireOp",EDGE,"E1.top");var subQ2=makeQuery(id+"F0.imprint","IMPRINT",VERTEX,{"derivedFrom":subQ0});Q40=makeQuery(id+"F0.imprint","IMPRINT",FACE,{"disambiguationData":[TD([[makeQuery(id+"F0.imprint","IMPRINT",EDGE,{"disambiguationData":[TD([[subQ2,1.0]])],"derivedFrom":subQ0}),-1.0]])]});}
            var Q41;
            {var subQ3=sQuery(id+"F0.wireOp",EDGE,"E86.bottom");var subQ7=makeQuery(id+"F0.imprint","IMPRINT",VERTEX,{"derivedFrom":subQ3});Q41=makeQuery(id+"F0.imprint","IMPRINT",FACE,{"disambiguationData":[TD([[makeQuery(id+"F0.imprint","IMPRINT",EDGE,{"disambiguationData":[TD([[subQ7,-1.0]])],"derivedFrom":subQ3}),1.0]])]});}
            var Q42;
            {var subQ0=sQuery(id+"F0.wireOp",EDGE,"E46.left");var subQ3=makeQuery(id+"F0.imprint","IMPRINT",VERTEX,{"disambiguationData":[OD(0.0)],"derivedFrom":subQ0});Q42=makeQuery(id+"F0.imprint","IMPRINT",FACE,{"disambiguationData":[TD([[makeQuery(id+"F0.imprint","IMPRINT",EDGE,{"disambiguationData":[TD([[subQ3,-1.0]])],"derivedFrom":subQ0}),-1.0]])]});}
            var Q43;
            {var subQ0=sQuery(id+"F0.wireOp",EDGE,"E46.right");var subQ1=makeQuery(id+"F0.imprint","INTERSECT",VERTEX,{"derivedFrom":[sQuery(id+"F0.wireOp",EDGE,"E43.top"),subQ0]});Q43=makeQuery(id+"F0.imprint","IMPRINT",FACE,{"disambiguationData":[TD([[makeQuery(id+"F0.imprint","IMPRINT",EDGE,{"disambiguationData":[TD([[subQ1,1.0]])],"derivedFrom":subQ0}),-1.0]])]});}
            var Q44;
            {var subQ0=sQuery(id+"F0.wireOp",EDGE,"E46.right");var subQ1=sQuery(id+"F0.wireOp",EDGE,"E43.top");var subQ2=makeQuery(id+"F0.imprint","INTERSECT",VERTEX,{"derivedFrom":[subQ1,subQ0]});Q44=makeQuery(id+"F0.imprint","IMPRINT",FACE,{"disambiguationData":[TD([[makeQuery(id+"F0.imprint","IMPRINT",EDGE,{"disambiguationData":[TD([[subQ2,1.0]])],"derivedFrom":subQ1}),1.0]])]});}
            var Q45;
            {var subQ0=sQuery(id+"F0.wireOp",EDGE,"E46.right");var subQ1=sQuery(id+"F0.wireOp",EDGE,"E43.top");var subQ2=makeQuery(id+"F0.imprint","INTERSECT",VERTEX,{"derivedFrom":[subQ1,subQ0]});Q45=makeQuery(id+"F0.imprint","IMPRINT",FACE,{"disambiguationData":[TD([[makeQuery(id+"F0.imprint","IMPRINT",EDGE,{"disambiguationData":[TD([[subQ2,1.0]])],"derivedFrom":subQ1}),-1.0]])]});}
            var Q46;
            {var subQ1=sQuery(id+"F0.wireOp",EDGE,"E38.bottom");Q46=makeQuery(id+"F0.imprint","IMPRINT",FACE,{"disambiguationData":[TD([[makeQuery(id+"F0.imprint","IMPRINT",EDGE,{"derivedFrom":subQ1}),1.0]])]});}
            var Q47;
            {var subQ0=sQuery(id+"F0.wireOp",EDGE,"E38.right");var subQ1=sQuery(id+"F0.wireOp",EDGE,"E38.top");var subQ2=makeQuery(id+"F0.imprint","INTERSECT",VERTEX,{"derivedFrom":[subQ1,subQ0]});Q47=makeQuery(id+"F0.imprint","IMPRINT",FACE,{"disambiguationData":[TD([[makeQuery(id+"F0.imprint","IMPRINT",EDGE,{"disambiguationData":[TD([[subQ2,1.0]])],"derivedFrom":subQ1}),1.0]])]});}
            var Q48;
            {var subQ0=sQuery(id+"F0.wireOp",EDGE,"E38.right");var subQ1=sQuery(id+"F0.wireOp",EDGE,"E38.top");var subQ2=makeQuery(id+"F0.imprint","INTERSECT",VERTEX,{"derivedFrom":[subQ1,subQ0]});Q48=makeQuery(id+"F0.imprint","IMPRINT",FACE,{"disambiguationData":[TD([[makeQuery(id+"F0.imprint","IMPRINT",EDGE,{"disambiguationData":[TD([[subQ2,1.0]])],"derivedFrom":subQ1}),-1.0]])]});}
            var Q49;
            {var subQ7=sQuery(id+"F0.wireOp",EDGE,"E10.bottom");Q49=makeQuery(id+"F0.imprint","IMPRINT",FACE,{"disambiguationData":[TD([[makeQuery(id+"F0.imprint","IMPRINT",EDGE,{"derivedFrom":subQ7}),-1.0]])]});}
            var Q50;
            {var subQ1=sQuery(id+"F0.wireOp",EDGE,"E2");Q50=makeQuery(id+"F0.imprint","IMPRINT",FACE,{"disambiguationData":[TD([[makeQuery(id+"F0.imprint","IMPRINT",EDGE,{"derivedFrom":subQ1}),-1.0]])]});}
            var Q51;
            {var subQ1=sQuery(id+"F0.wireOp",EDGE,"E26.bottom");Q51=makeQuery(id+"F0.imprint","IMPRINT",FACE,{"disambiguationData":[TD([[makeQuery(id+"F0.imprint","IMPRINT",EDGE,{"derivedFrom":subQ1}),-1.0]])]});}
            var Q52;
            {var subQ0=sQuery(id+"F0.wireOp",EDGE,"E26.right");var subQ1=sQuery(id+"F0.wireOp",EDGE,"E26.top");var subQ2=makeQuery(id+"F0.imprint","INTERSECT",VERTEX,{"derivedFrom":[subQ1,subQ0]});Q52=makeQuery(id+"F0.imprint","IMPRINT",FACE,{"disambiguationData":[TD([[makeQuery(id+"F0.imprint","IMPRINT",EDGE,{"disambiguationData":[TD([[subQ2,1.0]])],"derivedFrom":subQ1}),1.0]])]});}
            var Q53;
            {var subQ0=sQuery(id+"F0.wireOp",EDGE,"E26.right");var subQ1=sQuery(id+"F0.wireOp",EDGE,"E26.top");var subQ2=makeQuery(id+"F0.imprint","INTERSECT",VERTEX,{"derivedFrom":[subQ1,subQ0]});Q53=makeQuery(id+"F0.imprint","IMPRINT",FACE,{"disambiguationData":[TD([[makeQuery(id+"F0.imprint","IMPRINT",EDGE,{"disambiguationData":[TD([[subQ2,1.0]])],"derivedFrom":subQ1}),-1.0]])]});}
            var Q54;
            {var subQ0=sQuery(id+"F0.wireOp",EDGE,"E25.right");var subQ1=sQuery(id+"F0.wireOp",EDGE,"E25.top");var subQ2=makeQuery(id+"F0.imprint","INTERSECT",VERTEX,{"derivedFrom":[subQ1,subQ0]});Q54=makeQuery(id+"F0.imprint","IMPRINT",FACE,{"disambiguationData":[TD([[makeQuery(id+"F0.imprint","IMPRINT",EDGE,{"disambiguationData":[TD([[subQ2,1.0]])],"derivedFrom":subQ1}),1.0]])]});}
            var Q55;
            {var subQ0=sQuery(id+"F0.wireOp",EDGE,"E25.right");var subQ1=sQuery(id+"F0.wireOp",EDGE,"E25.top");var subQ2=makeQuery(id+"F0.imprint","INTERSECT",VERTEX,{"derivedFrom":[subQ1,subQ0]});Q55=makeQuery(id+"F0.imprint","IMPRINT",FACE,{"disambiguationData":[TD([[makeQuery(id+"F0.imprint","IMPRINT",EDGE,{"disambiguationData":[TD([[subQ2,1.0]])],"derivedFrom":subQ1}),-1.0]])]});}
            var Q56;
            {var subQ1=sQuery(id+"F0.wireOp",EDGE,"E25.bottom");Q56=makeQuery(id+"F0.imprint","IMPRINT",FACE,{"disambiguationData":[TD([[makeQuery(id+"F0.imprint","IMPRINT",EDGE,{"derivedFrom":subQ1}),1.0]])]});}
            extrude(context, id + "F1", {"entities" : qUnion([Q0, Q1, Q2, Q3, Q4, Q5, Q6, Q7, Q8, Q9, Q10, Q11, Q12, Q13, Q14, Q15, Q16, Q17, Q18, Q19, Q20, Q21, Q22, Q23, Q24, Q25, Q26, Q27, Q28, Q29, Q30, Q31, Q32, Q33, Q34, Q35, Q36, Q37, Q38, Q39, Q40, Q41, Q42, Q43, Q44, Q45, Q46, Q47, Q48, Q49, Q50, Q51, Q52, Q53, Q54, Q55, Q56]), "depth" : 2 * mm, "offsetDistance" : 25 * mm});
        }
    });
